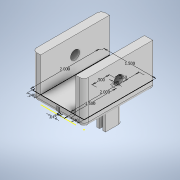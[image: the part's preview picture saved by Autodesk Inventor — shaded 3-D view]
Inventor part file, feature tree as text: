
AUTODESK INVENTOR PART (.ipt)
format: ipt  version: 2020 (Build 240168000, 168)  size: 184,320 bytes
history: native  units: in
note: dims shown in document units (in); Inventor stores cm internally (conversion verified against a paired STEP export)
features: extrude x4, sketch x3, fillet x2, hole x1
ambient origin geometry x8: Origin, YZ Plane, XZ Plane, XY Plane, X Axis, Y Axis, Z Axis, Center Point
bodies: Solid1 (feature_tree)
feature tree (10):
  sketch  "Sketch1"  dims[d0=1.5in d1=2.0in]
  extrude  "Extrusion1"  Depth=2.0in
  extrude  "Extrusion2"  Depth=0.24in
  sketch  "Sketch2"  dims[d2=0.24in d3=0.24in]
  extrude  "Extrusion3"  Depth=1.0in TaperAngle=0.0deg
  extrude  "Extrusion4"  Depth=0.25in TaperAngle=0.0deg
  fillet  "Fillet1"  Radius=0.045in
  fillet  "Fillet2"  Radius=1.5in
  hole  "Hole1"  [1 undecoded]
  sketch  "Sketch3"  dims[d4=2.0in d5=1.0in d6=0.0in d7=0.25in d8=0.0in d9=0.045in d10=1.5in d11=0.045in d12=0.25in d13=0.5in d14=0.2in d15=0.0in d16=1.0in d17=0.0in d18=0.125in d19=0.125in d20=0.5in d21=0.266in d22=0.75in d23=0.507in d24=0.25in d25=0.5635in d26=0.125in d27=0.0in]
note: 1 required parameter value undecoded (feature->parameter linkage not recoverable at this tier; creation-order binding heuristic only, values carry confidence <= 0.55)
